# Revit family: BuroSeating_Buro Diablo
name_source: partatom
category: Furniture
units: mm (PartAtom-declared; Revit-internal decimal feet)

## family parameters
Always vertical = Yes
Cut with Voids When Loaded = No
OmniClass Number = 23.40.70.14.64.11
OmniClass Title = Office Furniture
Room Calculation Point = No
Shared = Yes
Work Plane-Based = No

## types (8) — shared parameters
ArmRestMaterial = BuroSeating_Aluminium_Black
Assembly Code = E2020
BackFrameMaterial = BuroSeating_Aluminium_Black
BackPanelMaterial = BuroSeating_PU_Black
BackRestMaterial = <By Category>
BackSupportMaterial = BuroSeating_Aluminium_Black
BaseMaterial = BuroSeating_Aluminium_Brushed_Black
CastorMaterial = BuroSeating_Aluminium_Black
CastorWheelMaterial = BuroSeating_Aluminium_Black
FrameMaterial = BuroSeating_Aluminium_Black
Manufacturer = Buro Seating
NominalDepth = 630 mm
NominalSeatHeight = 435-530h
NominalWidth = 650 mm  [stored 2.13255 ft]
ProductGroup = Diablo
ProductPageURL AU = https://buroseating.com
ProductPageURL NZ = https://buroseating.co.nz
ProductRange = Buro
SeatDepth = 480 mm  [stored 1.5748 ft]
SeatLeverFrameMaterial = BuroSeating_Aluminium_Black
SeatSupportMaterial = BuroSeating_Aluminium_Black
SeatWidth = 500 mm  [stored 1.64042 ft]
TopLiftMaterial = BuroSeating_Metal_Chrome_Semi-Polished
Type Comments = Seat Height 435-530mm High
URL = https://buroseating.co.nz
URL AU = https://buroseating.com
WarrantyDescription = Full 5 year guarantee (excluding upholstery)
zero-valued in all types: Default Elevation

## per-type parameters (varying)
| type | Description | HighBack | MediumBack | Model | NominalHeight | SeatArms | SeatMaterial |
| Buro Diablo 136-PU3 Black PU - Medium Back | Buro Diablo Black PU Medium Back | No | Yes | 136-PU3 Black PU | 650 mm  [stored 2.13255 ft] | No | BuroSeating_PU_Black |
| Buro Diablo 136-PU3 Black PU - High Back | Buro Diablo Black PU High Back | Yes | No | 136-PU3 Black PU | 1085 mm | No | BuroSeating_PU_Black |
| Buro Diablo 136-M2 Charcoal Fabric Mesh - High Back | Buro Diablo Charcoal Fabric Mesh High Back | Yes | No | 136-M2 Charcoal Fabric Mesh | 1085 mm | No | BuroSeating_Fabric_Charcoal |
| Buro Diablo 136-M2 Charcoal Fabric Mesh - Medium Back | Buro Diablo Charcoal Fabric Mesh Medium Back | No | Yes | 136-M2 Charcoal Fabric Mesh | 650 mm  [stored 2.13255 ft] | No | BuroSeating_Fabric_Charcoal |
| Buro Diablo 136-M2 Charcoal Fabric Mesh - High Back w Arms | Buro Diablo Charcoal Fabric Mesh High Back | Yes | No | 136-M2 Charcoal Fabric Mesh with Arms | 1085 mm | Yes | BuroSeating_Fabric_Charcoal |
| Buro Diablo 136-M2 Charcoal Fabric Mesh - Medium Back w Arms | Buro Diablo Charcoal Fabric Mesh Medium Back | No | Yes | 136-M2 Charcoal Fabric Mesh with Arms | 650 mm  [stored 2.13255 ft] | Yes | BuroSeating_Fabric_Charcoal |
| Buro Diablo 136-PU3 Black PU - High Back w Arms | Buro Diablo Black PU High Back | Yes | No | 136-PU3 Black PU with Arms | 1085 mm | Yes | BuroSeating_PU_Black |
| Buro Diablo 136-PU3 Black PU - Medium Back w Arms | Buro Diablo Black PU Medium Back | No | Yes | 136-PU3 Black PU with Arms | 650 mm  [stored 2.13255 ft] | Yes | BuroSeating_PU_Black |

note: [stored X ft] marks values corroborated as IEEE doubles in the binary element streams (Revit-internal decimal feet)

## geometry (parser evidence)
native form markers: Sweep x11
no freeform markers — native parametric forms only
